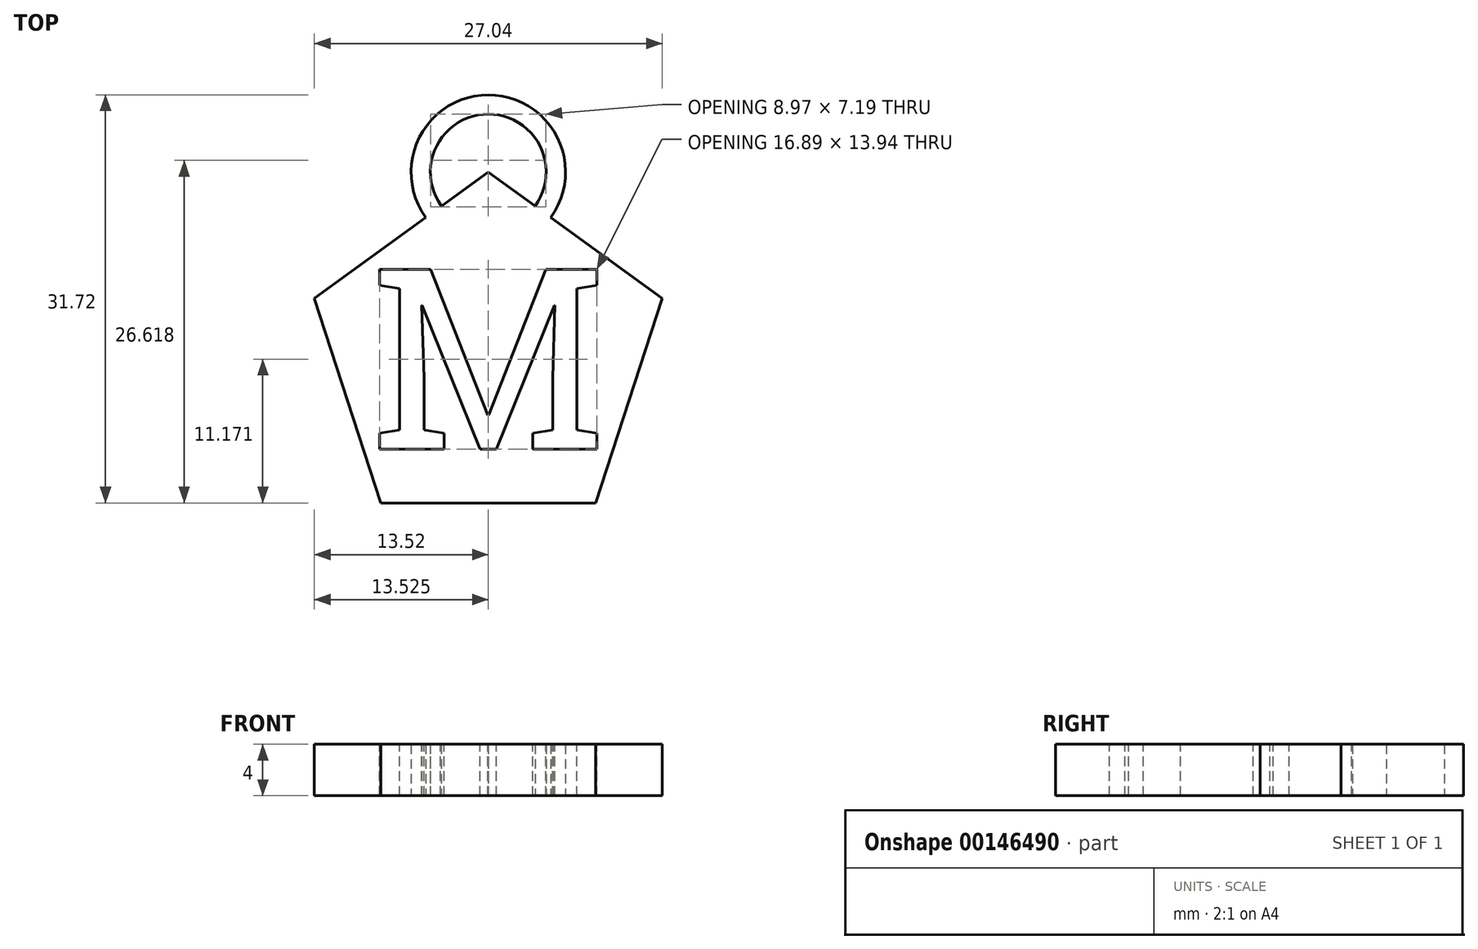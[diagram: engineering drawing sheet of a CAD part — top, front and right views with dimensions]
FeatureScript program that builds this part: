
annotation { "Feature Type Name" : "Feature", "Feature Type Description" : "" }
export const myFeature = defineFeature(function(context is Context, id is Id, definition is map)
    precondition{}
    {
        {
            var Q0;
            Q0=qCreatedBy(makeId("Top.planeOp"),FACE);
            var sketch = newSketch(context, id + "F0", { "sketchPlane" : qUnion([Q0])});
            skCircle(sketch, "E0.cCircle", {"center": v(-26.08, 11.5) * mm, "radius": 11.5 * mm, "construction": true});
            skLineSegment(sketch, "E0.0", {"start": v(-12.56, 15.9) * mm, "end": v(-17.72, 0) * mm});
            skLineSegment(sketch, "E0.1", {"start": v(-17.72, 0) * mm, "end": v(-34.43, 0) * mm});
            skLineSegment(sketch, "E0.2", {"start": v(-34.43, 0) * mm, "end": v(-39.6, 15.9) * mm});
            skLineSegment(sketch, "E0.3", {"start": v(-39.6, 15.9) * mm, "end": v(-26.08, 25.71) * mm});
            skLineSegment(sketch, "E0.4", {"start": v(-26.08, 25.71) * mm, "end": v(-12.56, 15.9) * mm});
            skPoint(sketch, "E0.0.midPoint", {"position": v(-15.14, 7.95) * mm});
            skCircle(sketch, "E1.cCircle", {"center": v(-26.08, 11.5) * mm, "radius": 10.75 * mm, "construction": true});
            skLineSegment(sketch, "E1.0", {"start": v(-13.43, 15.57) * mm, "end": v(-18.3, 0.73) * mm});
            skLineSegment(sketch, "E1.1", {"start": v(-18.3, 0.73) * mm, "end": v(-33.92, 0.77) * mm});
            skLineSegment(sketch, "E1.2", {"start": v(-33.92, 0.77) * mm, "end": v(-38.7, 15.65) * mm});
            skLineSegment(sketch, "E1.3", {"start": v(-38.7, 15.65) * mm, "end": v(-26.04, 24.79) * mm});
            skLineSegment(sketch, "E1.4", {"start": v(-26.04, 24.79) * mm, "end": v(-13.43, 15.57) * mm});
            skPoint(sketch, "E1.0.midPoint", {"position": v(-15.87, 8.15) * mm});
            skSolve(sketch);
        }
        {
            var Q0;
            Q0=makeQuery(id+"F0.imprint","IMPRINT",FACE,{"disambiguationData":[TD([[makeQuery(id+"F0.imprint","IMPRINT",EDGE,{"derivedFrom":sQuery(id+"F0.wireOp",EDGE,"E0.0")}),-1.0]])]});
            extrude(context, id + "F1", {"entities" : qUnion([Q0]), "depth" : 2 * mm});
        }
        {
            var Q0;
            Q0=makeQuery(id+"F0.imprint","IMPRINT",FACE,{"disambiguationData":[TD([[makeQuery(id+"F0.imprint","IMPRINT",EDGE,{"derivedFrom":sQuery(id+"F0.wireOp",EDGE,"E1.0")}),-1.0]])]});
            extrude(context, id + "F2", {"entities" : qUnion([Q0]), "operationType" : NewBodyOperationType.ADD, "depth" : 2 * mm});
        }
        {
            var Q0;
            Q0=makeQuery(id+"F0.imprint","IMPRINT",FACE,{"disambiguationData":[TD([[makeQuery(id+"F0.imprint","IMPRINT",EDGE,{"derivedFrom":sQuery(id+"F0.wireOp",EDGE,"E0.0")}),-1.0]])]});
            extrude(context, id + "F3", {"entities" : qUnion([Q0]), "operationType" : NewBodyOperationType.ADD, "oppositeDirection" : true, "depth" : 2 * mm});
        }
        {
            var Q0;
            Q0=makeQuery(id+"F0.imprint","IMPRINT",FACE,{"disambiguationData":[TD([[makeQuery(id+"F0.imprint","IMPRINT",EDGE,{"derivedFrom":sQuery(id+"F0.wireOp",EDGE,"E1.0")}),-1.0]])]});
            extrude(context, id + "F4", {"entities" : qUnion([Q0]), "operationType" : NewBodyOperationType.ADD, "oppositeDirection" : true, "depth" : 2 * mm});
        }
        {
            var Q0;
            Q0=qCreatedBy(makeId("Top.planeOp"),FACE);
            var sketch = newSketch(context, id + "F5", { "sketchPlane" : qUnion([Q0])});
            skText(sketch, "E2", { "text": "M", "fontName": "RobotoSlab-Regular.ttf"});
            const initialGuessF5  = {"E2": [-0.03546, 0.0039, 1, 0, 0.014]};
            skSetInitialGuess(sketch, initialGuessF5);
            skSolve(sketch);
        }
        {
            var Q0;
            Q0=makeQuery(id+"F2.opExtrude","CAP_FACE",FACE,{"disambiguationData":[OSD([sQuery(id+"F0.wireOp",EDGE,"E1.0"),sQuery(id+"F0.wireOp",EDGE,"E1.1"),sQuery(id+"F0.wireOp",EDGE,"E1.2"),sQuery(id+"F0.wireOp",EDGE,"E1.3"),sQuery(id+"F0.wireOp",EDGE,"E1.4")])],"isStart":false});
            var sketch = newSketch(context, id + "F6", { "sketchPlane" : qUnion([Q0])});
            skText(sketch, "E3", { "text": "M", "fontName": "RobotoSlab-Regular.ttf"});
            const initialGuessF6  = {"E3": [-0.0352, 0.0042, 1, 0, 0.01412]};
            skSetInitialGuess(sketch, initialGuessF6);
            skSolve(sketch);
        }
        {
            var Q0;
            Q0=qCreatedBy(makeId("Top.planeOp"),FACE);
            var sketch = newSketch(context, id + "F7", { "sketchPlane" : qUnion([Q0])});
            skArc(sketch, "E4", {"start": v(-26.02, 31.71) * mm, "mid": v(-31.48, 28.32) * mm, "end": v(-30.74, 21.93) * mm});
            skArc(sketch, "E5", {"start": v(-26.02, 31.71) * mm, "mid": v(-20.65, 28.27) * mm, "end": v(-21.41, 21.94) * mm});
            skArc(sketch, "E6", {"start": v(-22.45, 23.06) * mm, "mid": v(-26.06, 30.21) * mm, "end": v(-29.73, 23.08) * mm});
            skLineSegment(sketch, "E7", {"start": v(-30.74, 21.93) * mm, "end": v(-29.73, 23.08) * mm});
            skLineSegment(sketch, "E8", {"start": v(-21.41, 21.94) * mm, "end": v(-22.45, 23.06) * mm});
            skSolve(sketch);
        }
        {
            var Q0;
            Q0 = qSketchRegion(id + "F7", true);
            extrude(context, id + "F8", {"entities" : qUnion([Q0]), "operationType" : NewBodyOperationType.ADD, "endBound" : BoundingType.SYMMETRIC, "depth" : 4 * mm});
        }
        {
            var Q0;
            Q0=makeQuery(id+"F6.imprint","IMPRINT",FACE,{"disambiguationData":[TD([[makeQuery(id+"F6.imprint","IMPRINT",EDGE,{"derivedFrom":sQuery(id+"F6.wireOp",EDGE,"E3.sketch_text.stroke-0")}),-1.0]])]});
            extrude(context, id + "F9", {"entities" : qUnion([Q0]), "operationType" : NewBodyOperationType.REMOVE, "oppositeDirection" : true, "depth" : 25 * mm});
        }
    });
